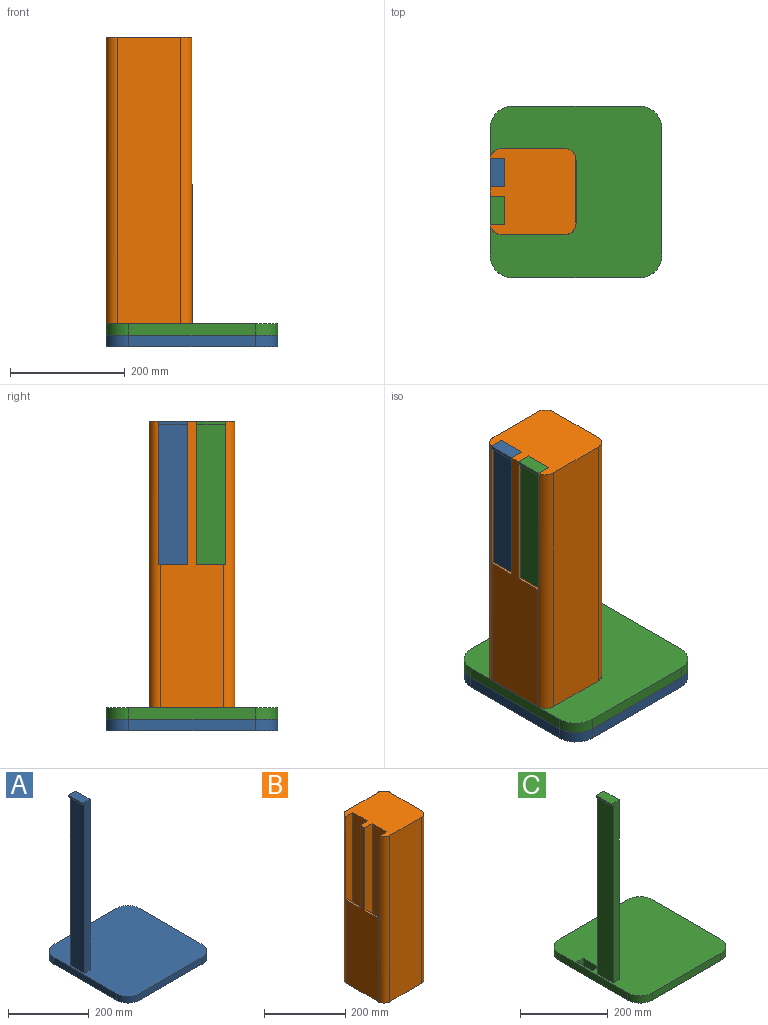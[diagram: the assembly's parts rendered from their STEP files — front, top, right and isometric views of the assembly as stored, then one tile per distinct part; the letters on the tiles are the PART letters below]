
ASSEMBLY  parts=3 mates=8
PART A: 17 faces, bbox 300x300x540 mm
  f0: plane 515x50mm, normal (-1,0,0), area 25750mm2, adj f1,f7,f8,f11
  f1: plane 300x300mm, normal (0,0,1), area 87626.5mm2, adj f0,f2,f3,f4,f5,f7,f8,f9
  f2: plane 220x20mm, normal (0,1,0), area 4400mm2, adj f1,f6,f13,f16
  f3: plane 220x20mm, normal (-1,0,0), area 4400mm2, adj f1,f6,f13,f14
  f4: plane 220x20mm, normal (0,-1,0), area 4400mm2, adj f1,f6,f14,f15
  f5: plane 220x20mm, normal (1,0,0), area 4400mm2, adj f1,f6,f15,f16
  f6: plane 300x300mm, normal (0,0,-1), area 88626.5mm2, adj f2,f3,f4,f5,f13,f14,f15,f16
  f7: plane 520x25mm, normal (0,1,0), area 10425mm2, adj f0,f1,f9,f10,f11,f12
  f8: plane 520x25mm, normal (0,-1,0), area 10425mm2, adj f0,f1,f9,f10,f11,f12
  f9: plane 520x50mm, normal (1,0,0), area 26000mm2, adj f1,f7,f8,f10
  f10: plane 50x25mm, normal (0,0,1), area 1250mm2, adj f7,f8,f9,f12
  f11: plane 50x5mm, normal (0,0,-1), area 250mm2, adj f0,f7,f8,f12
  f12: plane 50x5mm, normal (-1,0,0), area 250mm2, adj f7,f8,f10,f11
  f13: cylinder r=40mm len=40mm, axis (0,0,1), area 1256.6mm2, adj f1,f2,f3,f6
  f14: cylinder r=40mm len=40mm, axis (0,0,-1), area 1256.6mm2, adj f1,f3,f4,f6
  f15: cylinder r=40mm len=40mm, axis (0,0,1), area 1256.6mm2, adj f1,f4,f5,f6
  f16: cylinder r=40mm len=40mm, axis (0,0,-1), area 1256.6mm2, adj f1,f2,f5,f6
PART B: 20 faces, bbox 150x150x500 mm
  f0: plane 150x150mm, normal (0,0,-1), area 20156.6mm2, adj f1,f3,f4,f5,f6,f7,f8,f10
  f1: plane 500x110mm, normal (-1,0,0), area 31667mm2, adj f0,f2,f6,f9,f11,f13,f16,f19
  f2: plane 150x150mm, normal (0,0,1), area 19657.3mm2, adj f1,f3,f4,f5,f6,f7,f8,f10
  f3: plane 500x110mm, normal (0,-1,0), area 55000mm2, adj f0,f2,f16,f17
  f4: plane 500x110mm, normal (1,0,0), area 55000mm2, adj f0,f2,f17,f18
  f5: plane 500x110mm, normal (0,1,0), area 55000mm2, adj f0,f2,f18,f19
  f6: plane 500x25mm, normal (0,-1,0), area 11250mm2, adj f0,f1,f2,f8,f9,f15
  f7: plane 500x24.72mm, normal (0,1,0), area 11180mm2, adj f0,f2,f8,f9,f15,f16
  f8: plane 500x50mm, normal (-1,0,0), area 25000mm2, adj f0,f2,f6,f7
  f9: plane 50x5mm, normal (0,0,1), area 249.7mm2, adj f1,f6,f7,f15,f16
  f10: plane 500x24.72mm, normal (0,-1,0), area 11180mm2, adj f0,f2,f12,f13,f14,f19
  f11: plane 500x25mm, normal (0,1,0), area 11250mm2, adj f0,f1,f2,f12,f13,f14
  f12: plane 500x50mm, normal (-1,0,0), area 25000mm2, adj f0,f2,f10,f11
  f13: plane 50x5mm, normal (0,0,1), area 249.7mm2, adj f1,f10,f11,f14,f19
  f14: plane 250x50mm, normal (1,0,0), area 12500mm2, adj f0,f10,f11,f13
  f15: plane 250x50mm, normal (1,0,0), area 12500mm2, adj f0,f6,f7,f9
  f16: cylinder r=20mm len=500mm, axis (0,0,1), area 14870.6mm2, adj f0,f1,f2,f3,f7,f9
  f17: cylinder r=20mm len=500mm, axis (0,0,-1), area 15708mm2, adj f0,f2,f3,f4
  f18: cylinder r=20mm len=500mm, axis (0,0,1), area 15708mm2, adj f0,f2,f4,f5
  f19: cylinder r=20mm len=500mm, axis (0,0,-1), area 14870.6mm2, adj f0,f1,f2,f5,f10,f13
PART C: 21 faces, bbox 300x300x520 mm
  f0: plane 300x300mm, normal (0,0,1), area 86626.5mm2, adj f2,f3,f4,f5,f6,f7,f8,f9
  f1: plane 300x300mm, normal (0,0,-1), area 87626.5mm2, adj f3,f4,f5,f6,f13,f14,f15,f16
  f2: plane 495x50mm, normal (-1,0,0), area 24750mm2, adj f0,f7,f8,f11
  f3: plane 220x20mm, normal (0,1,0), area 4400mm2, adj f0,f1,f17,f20
  f4: plane 220x20mm, normal (-1,0,0), area 4400mm2, adj f0,f1,f17,f18
  f5: plane 220x20mm, normal (0,-1,0), area 4400mm2, adj f0,f1,f18,f19
  f6: plane 220x20mm, normal (1,0,0), area 4400mm2, adj f0,f1,f19,f20
  f7: plane 500x25mm, normal (0,1,0), area 10025mm2, adj f0,f2,f9,f10,f11,f12
  f8: plane 500x25mm, normal (0,-1,0), area 10025mm2, adj f0,f2,f9,f10,f11,f12
  f9: plane 500x50mm, normal (1,0,0), area 25000mm2, adj f0,f7,f8,f10
  f10: plane 50x25mm, normal (0,0,1), area 1250mm2, adj f7,f8,f9,f12
  f11: plane 50x5mm, normal (0,0,-1), area 250mm2, adj f2,f7,f8,f12
  f12: plane 50x5mm, normal (-1,0,0), area 250mm2, adj f7,f8,f10,f11
  f13: plane 20x20mm, normal (0,-1,0), area 400mm2, adj f0,f1,f14,f16
  f14: plane 50x20mm, normal (1,0,0), area 1000mm2, adj f0,f1,f13,f15
  f15: plane 20x20mm, normal (0,1,0), area 400mm2, adj f0,f1,f14,f16
  f16: plane 50x20mm, normal (-1,0,0), area 1000mm2, adj f0,f1,f13,f15
  f17: cylinder r=40mm len=40mm, axis (0,0,1), area 1256.6mm2, adj f0,f1,f3,f4
  f18: cylinder r=40mm len=40mm, axis (0,0,-1), area 1256.6mm2, adj f0,f1,f4,f5
  f19: cylinder r=40mm len=40mm, axis (0,0,1), area 1256.6mm2, adj f0,f1,f5,f6
  f20: cylinder r=40mm len=40mm, axis (0,0,-1), area 1256.6mm2, adj f0,f1,f3,f6
PLACE A rot(axis=(0.3,-0.85,-0.43),0deg) t=(-364.12,-723.75,2184.72)mm
PLACE B rot(axis=(0.3,-0.85,-0.43),0deg) t=(-439.12,-723.75,2224.72)mm
PLACE C rot(axis=(0.3,-0.85,-0.43),0deg) t=(-364.12,-723.75,2204.72)mm
MATE planar C.f9 <-> B.f8  axis (1,0,0) through (-489.12,-757.09,2474.72)mm
MATE planar C.f8 <-> B.f7  axis (0,-1,0) through (-499.16,-782.09,2475.34)mm
MATE parallel C.f11 <-> B.f9  axis (0,0,-1) through (-511.62,-757.09,2719.72)mm
MATE parallel B.f0 <-> C.f0  axis (0,0,-1) through (-433.17,-723.75,2224.72)mm
MATE planar A.f7 <-> B.f10  axis (0,1,0) through (-499.15,-665.42,2465.34)mm
MATE parallel C.f1 <-> A.f1  axis (0,0,-1) through (-362.58,-724.14,2204.72)mm
MATE planar A.f9 <-> B.f12  axis (1,0,0) through (-489.12,-690.42,2464.72)mm
MATE parallel A.f11 <-> B.f13  axis (0,0,-1) through (-511.62,-690.42,2719.72)mm
